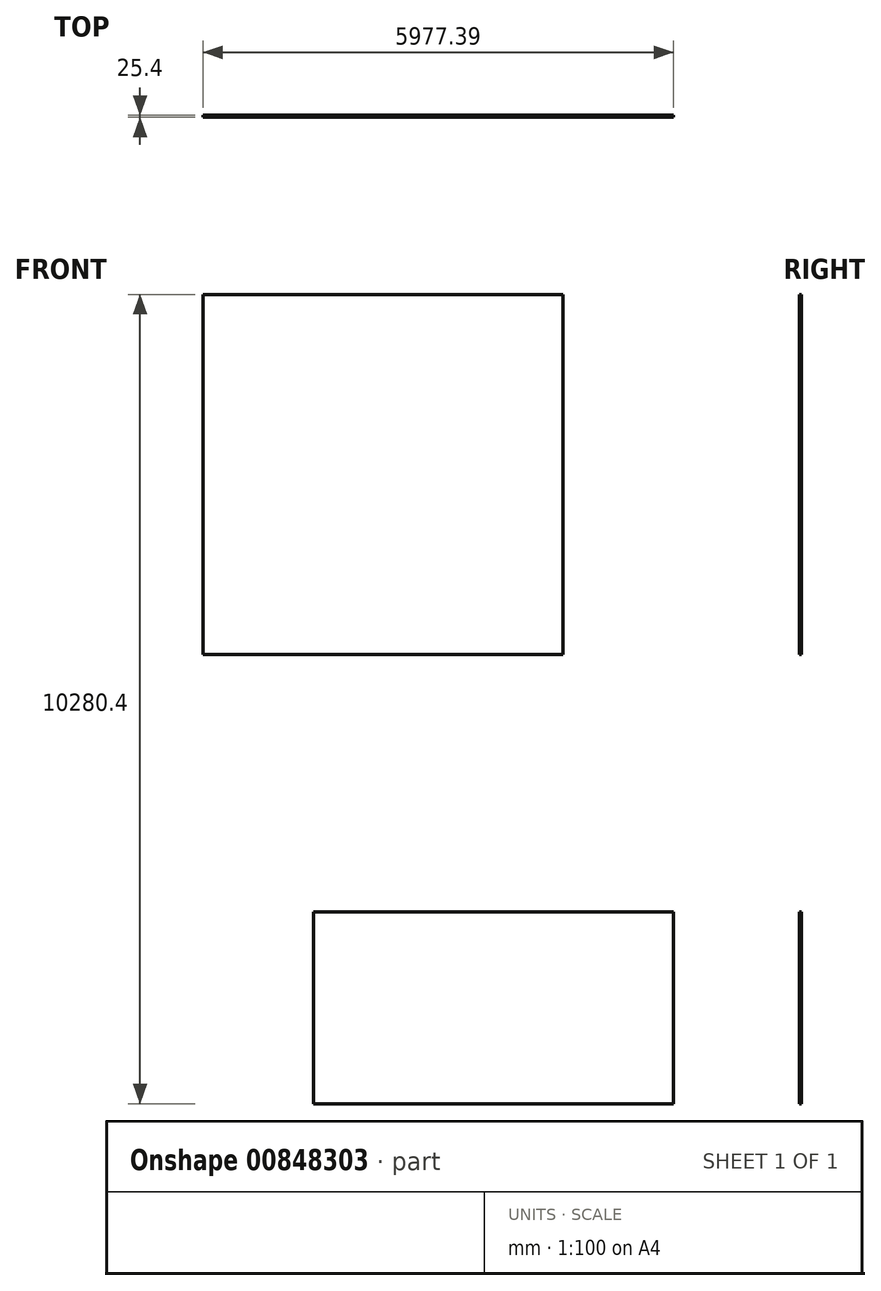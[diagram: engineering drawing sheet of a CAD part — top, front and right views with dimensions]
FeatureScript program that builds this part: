
annotation { "Feature Type Name" : "Feature", "Feature Type Description" : "" }
export const myFeature = defineFeature(function(context is Context, id is Id, definition is map)
    precondition{}
    {
        {
            var Q0;
            Q0=qCreatedBy(makeId("Front.planeOp"),FACE);
            var sketch = newSketch(context, id + "F0", { "sketchPlane" : qUnion([Q0])});
            skLineSegment(sketch, "E0.bottom", {"start": v(-159.64, 2374.41) * mm, "end": v(4412.36, 2374.41) * mm});
            skLineSegment(sketch, "E0.top", {"start": v(-159.64, -63.99) * mm, "end": v(4412.36, -63.99) * mm});
            skLineSegment(sketch, "E0.left", {"start": v(-159.64, 2374.41) * mm, "end": v(-159.64, -63.99) * mm});
            skLineSegment(sketch, "E0.right", {"start": v(4412.36, 2374.41) * mm, "end": v(4412.36, -63.99) * mm});
            skLineSegment(sketch, "E1.bottom", {"start": v(-159.64, 2374.41) * mm, "end": v(-159.64, 2374.41) * mm});
            skLineSegment(sketch, "E1.top", {"start": v(-159.64, -63.99) * mm, "end": v(-159.64, -63.99) * mm});
            skLineSegment(sketch, "E2.left", {"start": v(-159.64, 2374.41) * mm, "end": v(-159.64, 2171.21) * mm});
            skLineSegment(sketch, "E3.bottom", {"start": v(-1565.03, 10216.45) * mm, "end": v(3006.97, 10216.45) * mm});
            skLineSegment(sketch, "E3.top", {"start": v(-1565.03, 5644.45) * mm, "end": v(3006.97, 5644.45) * mm});
            skLineSegment(sketch, "E3.left", {"start": v(-1565.03, 10216.45) * mm, "end": v(-1565.03, 5644.45) * mm});
            skLineSegment(sketch, "E3.right", {"start": v(3006.97, 10216.45) * mm, "end": v(3006.97, 5644.45) * mm});
            skSolve(sketch);
        }
        {
            var Q0;
            Q0 = qSketchRegion(id + "F0", true);
            extrude(context, id + "F1", {"entities" : qUnion([Q0]), "depth" : 25.4 * mm, "offsetDistance" : 25.4 * mm});
        }
        {
            var Q0;
            Q0=makeQuery(id+"F0.imprint","IMPRINT",FACE,{"disambiguationData":[TD([[makeQuery(id+"F0.imprint","IMPRINT",EDGE,{"derivedFrom":sQuery(id+"F0.wireOp",EDGE,"E3.bottom")}),-1.0]])]});
            extrude(context, id + "F2", {"entities" : qUnion([Q0]), "operationType" : NewBodyOperationType.ADD, "depth" : 25.4 * mm, "offsetDistance" : 25.4 * mm});
        }
    });
